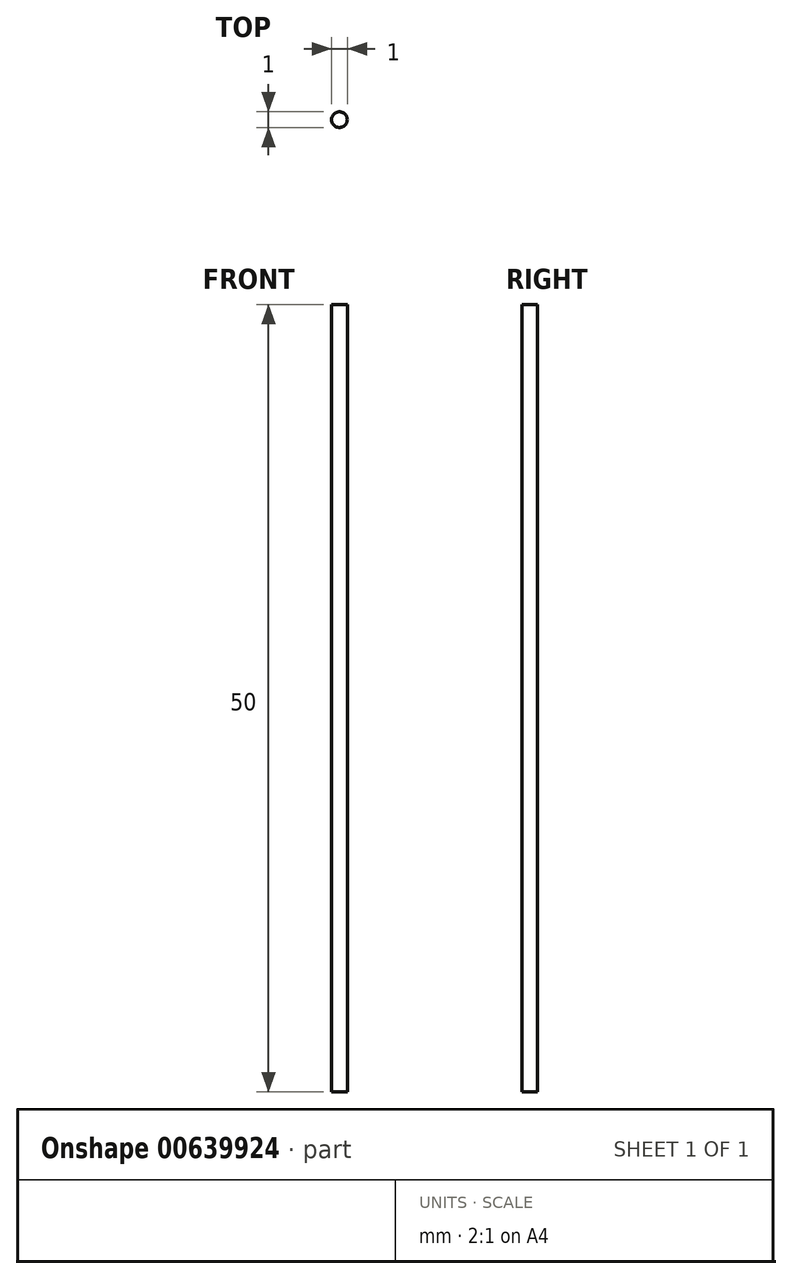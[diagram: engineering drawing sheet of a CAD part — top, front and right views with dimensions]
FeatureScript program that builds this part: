
annotation { "Feature Type Name" : "Feature", "Feature Type Description" : "" }
export const myFeature = defineFeature(function(context is Context, id is Id, definition is map)
    precondition{}
    {
        {
            var Q0;
            Q0=qCreatedBy(makeId("Top.planeOp"),FACE);
            var sketch = newSketch(context, id + "F0", { "sketchPlane" : qUnion([Q0])});
            skCircle(sketch, "E0", {"center": v(0, 0) * mm, "radius": 0.5 * mm});
            skSolve(sketch);
        }
        {
            var Q0;
            Q0 = qSketchRegion(id + "F0", true);
            extrude(context, id + "F1", {"entities" : qUnion([Q0]), "depth" : 50 * mm, "offsetDistance" : 25.4 * mm});
        }
    });
